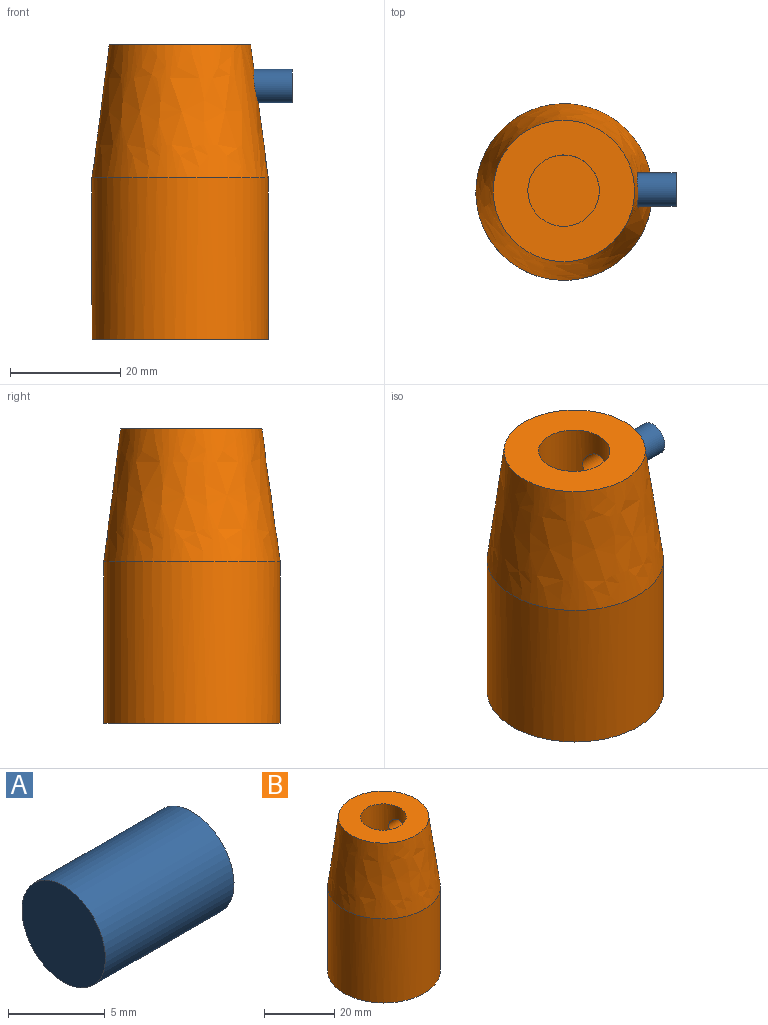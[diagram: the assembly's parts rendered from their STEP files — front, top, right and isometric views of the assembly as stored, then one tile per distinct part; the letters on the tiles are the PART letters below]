
ASSEMBLY  parts=2 mates=1
PART A: 10 faces, bbox 9.4x6.1x6.1 mm
  f0: cylinder r=3.05mm len=9.4mm, axis (-1,0,0), area 180mm2, adj f1,f2
  f1: plane 6.1x6.1mm, normal (1,0,0), area 16.6mm2, adj f0,f3,f4,f5,f6,f7,f8
  f2: plane 6.1x6.1mm, normal (-1,0,0), area 29.2mm2, adj f0
  f3: plane 1.88x1.27mm, normal (0,0.86,-0.52), area 2.8mm2, adj f1,f4,f8,f9
  f4: plane 1.93x1.27mm, normal (0,0.88,0.48), area 2.8mm2, adj f1,f3,f5,f9
  f5: plane 2.2x1.27mm, normal (0,0.02,1), area 2.8mm2, adj f1,f4,f6,f9
  f6: plane 1.88x1.27mm, normal (0,-0.86,0.52), area 2.8mm2, adj f1,f5,f7,f9
  f7: plane 1.93x1.27mm, normal (0,-0.88,-0.48), area 2.8mm2, adj f1,f6,f8,f9
  f8: plane 2.2x1.27mm, normal (0,-0.02,-1), area 2.8mm2, adj f1,f3,f7,f9
  f9: plane 4.4x3.85mm, normal (1,0,0), area 12.6mm2, adj f3,f4,f5,f6,f7,f8
PART B: 14 faces, bbox 32x32x53.3 mm
  f0: bspline ~31.98x31.98mm, area 2172mm2, adj f8,f11,f13
  f1: cylinder r=6.48mm len=17.78mm, axis (0,0,1), area 690.8mm2, adj f11,f12,f13
  f2: plane 29.21x14.81mm, normal (-1,0,0), area 432.6mm2, adj f3,f7,f9,f10
  f3: plane 29.21x12.83mm, normal (-0.5,0.87,0), area 432.6mm2, adj f2,f4,f9,f10
  f4: plane 29.21x12.83mm, normal (0.5,0.87,0), area 432.6mm2, adj f3,f5,f9,f10
  f5: plane 29.21x14.81mm, normal (1,0,0), area 432.6mm2, adj f4,f6,f9,f10
  f6: plane 29.21x12.83mm, normal (0.5,-0.87,0), area 432.6mm2, adj f5,f7,f9,f10
  f7: plane 29.21x12.83mm, normal (-0.5,-0.87,0), area 432.6mm2, adj f2,f6,f9,f10
  f8: cylinder r=16mm len=32mm, axis (0,0,-1), area 2936.9mm2, adj f0,f9
  f9: plane 32x32mm, normal (0,0,-1), area 234.5mm2, adj f2,f3,f4,f5,f6,f7,f8
  f10: plane 29.62x25.65mm, normal (0,0,-1), area 570mm2, adj f2,f3,f4,f5,f6,f7
  f11: plane 25.7x25.7mm, normal (0,0,1), area 385.1mm2, adj f0,f1
  f12: plane 12.95x12.95mm, normal (0,0,1), area 131.8mm2, adj f1
  f13: cylinder r=3.17mm len=8.76mm, axis (-1,0,0), area 152mm2, adj f0,f1
PLACE A t=(7.77,-13.96,69.75)mm
PLACE B t=(46.38,-2.09,0.15)mm fixed
MATE slider B.f13 <-> A.f0  axis (-1,0,0) through (11.12,28.78,46.02)mm
